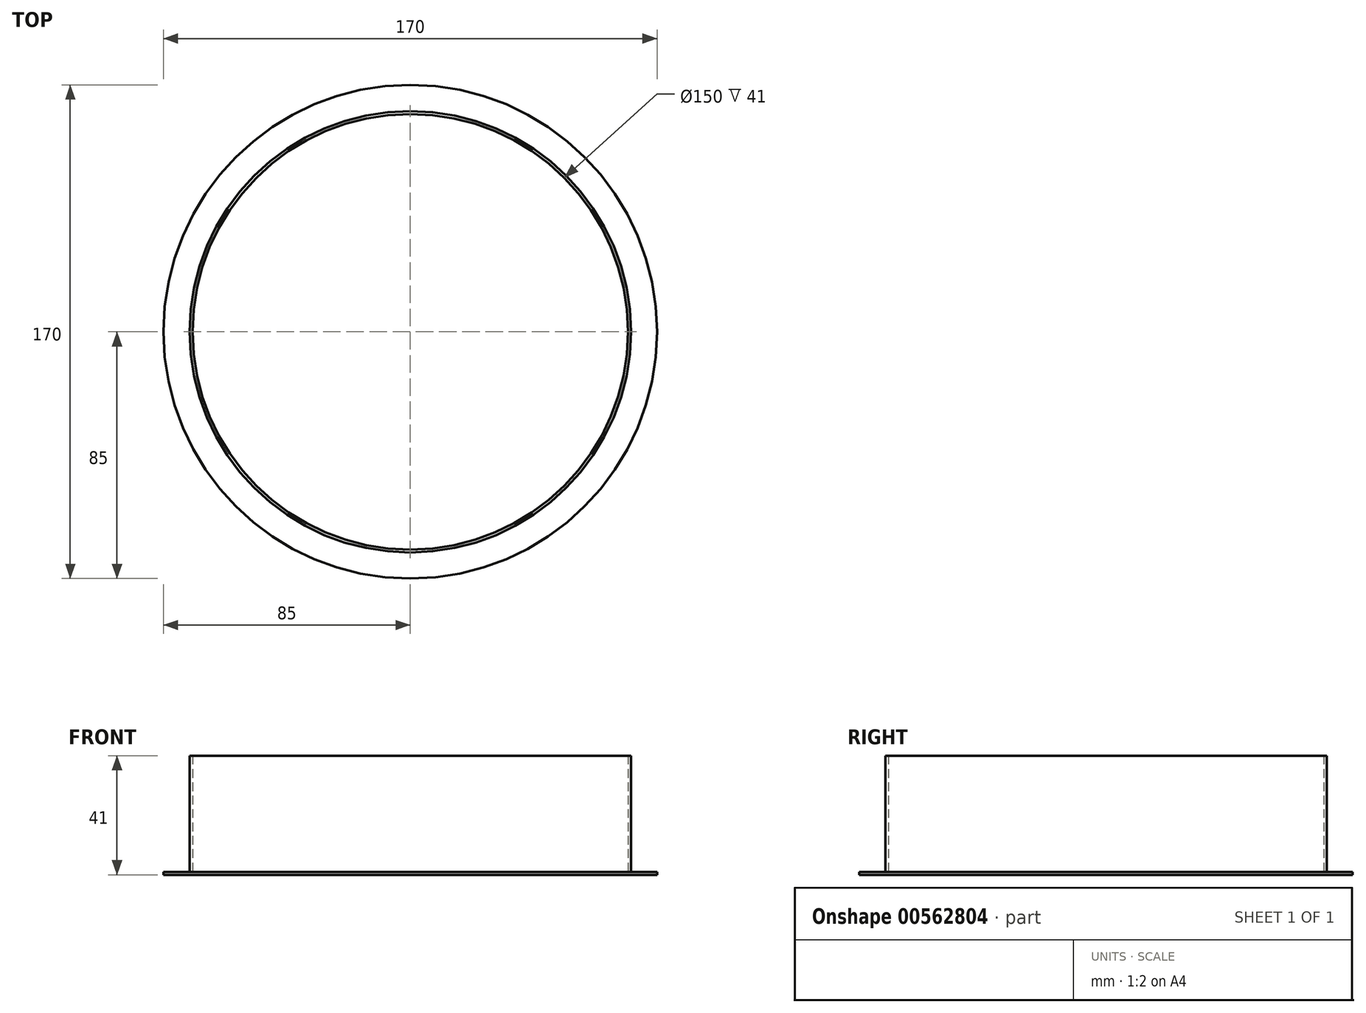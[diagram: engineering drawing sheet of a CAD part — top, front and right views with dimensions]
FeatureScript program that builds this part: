
annotation { "Feature Type Name" : "Feature", "Feature Type Description" : "" }
export const myFeature = defineFeature(function(context is Context, id is Id, definition is map)
    precondition{}
    {
        {
            var Q0;
            Q0=qCreatedBy(makeId("Right.planeOp"),FACE);
            var sketch = newSketch(context, id + "F0", { "sketchPlane" : qUnion([Q0])});
            skLineSegment(sketch, "E0", {"start": v(75, 0) * mm, "end": v(85, 0) * mm});
            skLineSegment(sketch, "E1", {"start": v(85, 0) * mm, "end": v(85, 1) * mm});
            skLineSegment(sketch, "E2", {"start": v(85, 1) * mm, "end": v(76, 1) * mm});
            skLineSegment(sketch, "E3", {"start": v(75, 0) * mm, "end": v(75, 41) * mm});
            skLineSegment(sketch, "E4", {"start": v(0, 41) * mm, "end": v(0, 0) * mm});
            skLineSegment(sketch, "E5.0", {"start": v(76, 41) * mm, "end": v(75, 41) * mm});
            skLineSegment(sketch, "E5.1", {"start": v(76, 1) * mm, "end": v(76, 41) * mm});
            skLineSegment(sketch, "E6", {"start": v(0, 0) * mm, "end": v(0, 51.54) * mm, "construction": true});
            skPoint(sketch, "E7.end.orphan", {"position": v(0, 19) * mm});
            skSolve(sketch);
        }
        {
            var Q0;
            {var subQ3=sQuery(id+"F0.wireOp",EDGE,"E3");Q0=makeQuery(id+"F0.imprint","IMPRINT",FACE,{"disambiguationData":[TD([[makeQuery(id+"F0.imprint","IMPRINT",EDGE,{"derivedFrom":subQ3}),-1.0]])]});}
            var Q1;
            {var subQ4=sQuery(id+"F0.wireOp",EDGE,"E0");Q1=makeQuery(id+"F0.imprint","IMPRINT",FACE,{"disambiguationData":[TD([[makeQuery(id+"F0.imprint","IMPRINT",EDGE,{"derivedFrom":subQ4}),1.0]])]});}
            var Q2;
            Q2=sQuery(id+"F0.wireOp",EDGE,"E6");
            revolve(context, id + "F1", {"entities" : qUnion([Q0, Q1]), "axis" : qUnion([Q2]), "revolveType" : RevolveType.FULL});
        }
    });
